# Revit family: Mercor - Przeciwpożarowa klapa odcinająca - mcr FID WING
name_source: partatom
category: Terminale wentylacyjne
revit_build: Autodesk Revit 2018 (Build: 20170927_1515(x64)
units: mm (PartAtom-declared; Revit-internal decimal feet)

## family parameters
Obiekt nadrzędny = Powierzchnia
Punkt obliczania pomieszczeń = Nie
Tnij formami wycięć po wczytaniu = Nie
Typ części = Normalny
Współdzielony = Nie
Wymiar okrągłego złącza = Użyj średnicy

## types (4) — shared parameters
Klasyfikacja obciążenia = Inne
Materiał = Mercor - blacha stalowa malowana proszkowo
Moc pozorna = 0 VA
Model = mcr FID WING
Napięcie = 0 V
Nazwa sterowania = RST
O = 60 mm  [stored 0.19685 ft]
OD = 10 mm  [stored 0.0328084 ft]
OK = 42.8 mm  [stored 0.14042 ft]
Opis sterowania = Mechanizm typu RST, złożony ze sprężyny napędowej oraz wyzwalacza topikowego
Producent = MERCOR S.A.
SC = 7 mm  [stored 0.0229659 ft]
URL = www.mercor.com.pl
Wysokość = 50 mm  [stored 0.164042 ft]
Wysokość otworu montażowego = 150 mm
zero-valued in all types: Domyślna rzędna

## per-type parameters (varying)
| type | A | D1 | D2 | D2.2 | DI | GK | LO | Powierzchnia czynna | Promień | Przekrój kanału | Waga | Średnica nominalna | Średnica otworu montażowego |
| mcr FID WING Ø100 | 21 mm  [stored 0.0688976 ft] | 100 mm  [stored 0.328084 ft] | 149 mm  [stored 0.488845 ft] | 74.5 mm  [stored 0.244423 ft] | 86 mm  [stored 0.282152 ft] | 7 mm  [stored 0.0229659 ft] | 36 mm | 0.0020 m² | 50 mm  [stored 0.164042 ft] | 0.0080 m² | 0.20 kg | 100 mm | 150 mm |
| mcr FID WING Ø125 | 34 mm | 125 mm  [stored 0.410105 ft] | 169 mm  [stored 0.554462 ft] | 84.5 mm  [stored 0.277231 ft] | 111 mm | 7.23 mm | 48.27 mm | 0.0040 m² | 62.5 mm  [stored 0.205052 ft] | 0.0120 m² | 0.30 kg | 125 mm | 175 mm  [stored 0.574147 ft] |
| mcr FID WING Ø160 | 51 mm | 160 mm  [stored 0.524934 ft] | 195 mm  [stored 0.639764 ft] | 97.5 mm  [stored 0.319882 ft] | 146 mm  [stored 0.479003 ft] | 7.23 mm | 65.77 mm | 0.0100 m² | 80 mm  [stored 0.262467 ft] | 0.0200 m² | 0.40 kg | 160 mm | 210 mm  [stored 0.688976 ft] |
| mcr FID WING Ø200 | 72 mm  [stored 0.23622 ft] | 200 mm  [stored 0.656168 ft] | 240 mm  [stored 0.787402 ft] | 120 mm  [stored 0.393701 ft] | 186 mm  [stored 0.610236 ft] | 11 mm  [stored 0.0360892 ft] | 82 mm  [stored 0.269029 ft] | 0.0170 m² | 100 mm  [stored 0.328084 ft] | 0.0310 m² | 0.60 kg | 200 mm | 250 mm  [stored 0.82021 ft] |

note: [stored X ft] marks values corroborated as IEEE doubles in the binary element streams (Revit-internal decimal feet)
